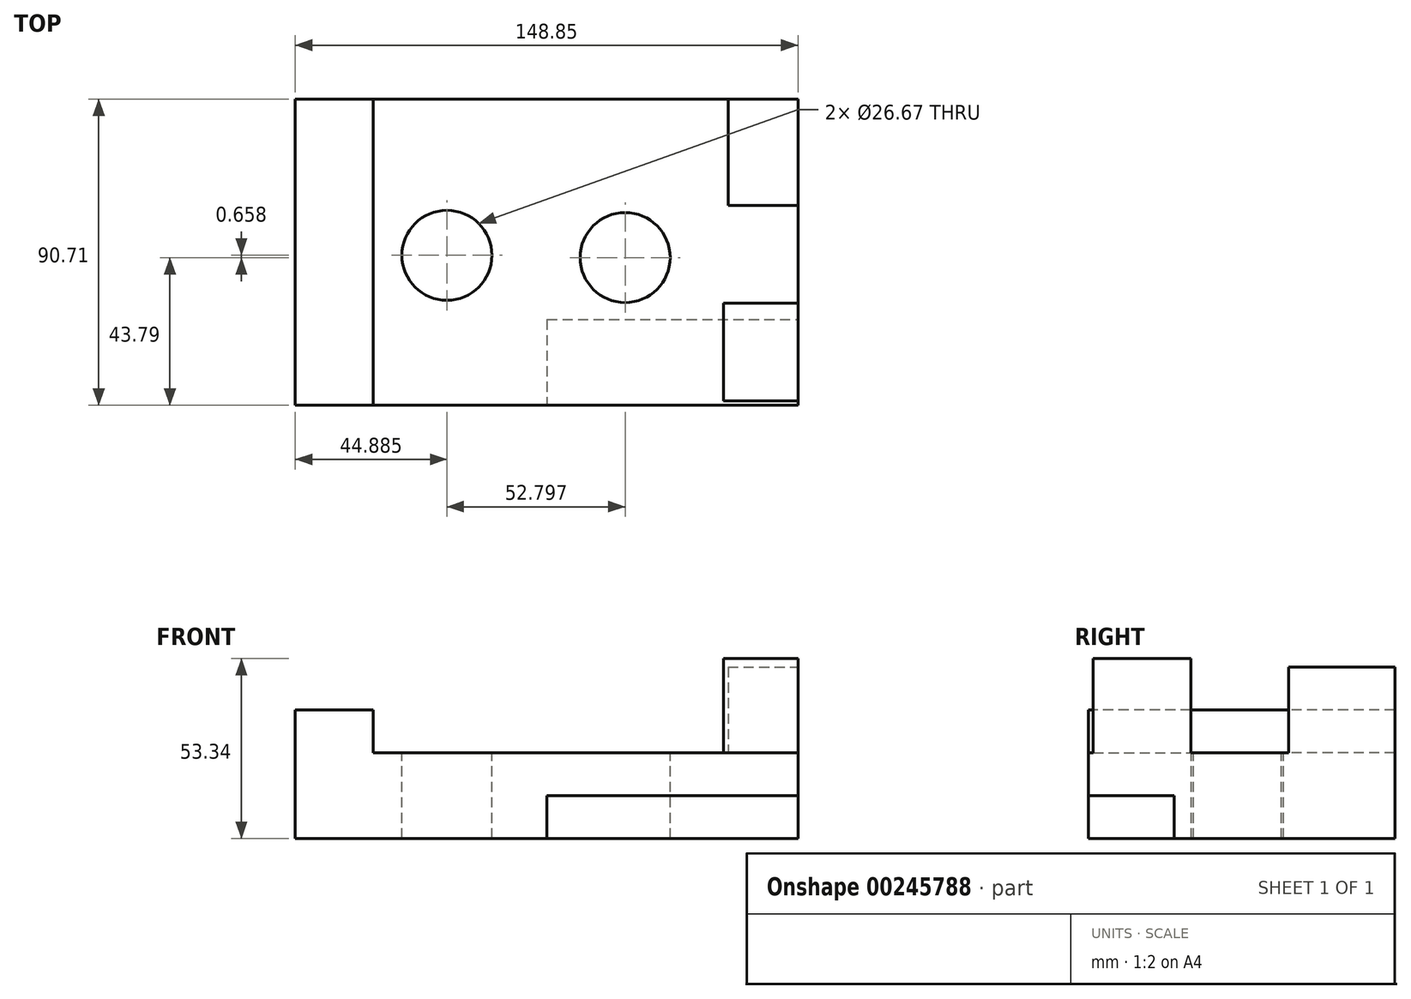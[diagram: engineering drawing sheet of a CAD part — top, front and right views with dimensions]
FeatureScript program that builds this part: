
annotation { "Feature Type Name" : "Feature", "Feature Type Description" : "" }
export const myFeature = defineFeature(function(context is Context, id is Id, definition is map)
    precondition{}
    {
        {
            var Q0;
            Q0=qCreatedBy(makeId("Top.planeOp"),FACE);
            var sketch = newSketch(context, id + "F0", { "sketchPlane" : qUnion([Q0])});
            skLineSegment(sketch, "E0.bottom", {"start": v(-74.54, 36.98) * mm, "end": v(74.31, 36.98) * mm});
            skLineSegment(sketch, "E0.top", {"start": v(-74.54, -53.73) * mm, "end": v(74.31, -53.73) * mm});
            skLineSegment(sketch, "E0.left", {"start": v(-74.54, 36.98) * mm, "end": v(-74.54, -53.73) * mm});
            skLineSegment(sketch, "E0.right", {"start": v(74.31, 36.98) * mm, "end": v(74.31, -53.73) * mm});
            skSolve(sketch);
        }
        {
            var Q0;
            Q0=makeQuery(id+"F0.imprint","IMPRINT",FACE,{"disambiguationData":[TD([[makeQuery(id+"F0.imprint","IMPRINT",EDGE,{"derivedFrom":sQuery(id+"F0.wireOp",EDGE,"E0.bottom")}),-1.0]])]});
            extrude(context, id + "F1", {"entities" : qUnion([Q0]), "depth" : 25.4 * mm});
        }
        {
            var Q0;
            Q0=makeQuery(id+"F1.opExtrude","SWEPT_FACE",FACE,{"disambiguationData":[OSD([sQuery(id+"F0.wireOp",EDGE,"E0.top")])]});
            var sketch = newSketch(context, id + "F2", { "sketchPlane" : qUnion([Q0])});
            skLineSegment(sketch, "E1.bottom", {"start": v(0, 0) * mm, "end": v(74.31, 0) * mm});
            skLineSegment(sketch, "E1.top", {"start": v(0, 12.7) * mm, "end": v(74.31, 12.7) * mm});
            skLineSegment(sketch, "E1.left", {"start": v(0, 0) * mm, "end": v(0, 12.7) * mm});
            skLineSegment(sketch, "E1.right", {"start": v(74.31, 0) * mm, "end": v(74.31, 12.7) * mm});
            skSolve(sketch);
        }
        {
            var Q0;
            Q0=makeQuery(id+"F2.imprint","IMPRINT",FACE,{"disambiguationData":[TD([[makeQuery(id+"F2.imprint","IMPRINT",EDGE,{"derivedFrom":sQuery(id+"F2.wireOp",EDGE,"E1.bottom")}),1.0]])]});
            extrude(context, id + "F3", {"entities" : qUnion([Q0]), "operationType" : NewBodyOperationType.REMOVE, "oppositeDirection" : true, "depth" : 25.4 * mm});
        }
        {
            var Q0;
            Q0=makeQuery(id+"F1.opExtrude","CAP_FACE",FACE,{"disambiguationData":[OSD([sQuery(id+"F0.wireOp",EDGE,"E0.bottom"),sQuery(id+"F0.wireOp",EDGE,"E0.top"),sQuery(id+"F0.wireOp",EDGE,"E0.left"),sQuery(id+"F0.wireOp",EDGE,"E0.right")])],"isStart":false});
            var sketch = newSketch(context, id + "F4", { "sketchPlane" : qUnion([Q0])});
            skLineSegment(sketch, "E2.bottom", {"start": v(-74.54, 36.98) * mm, "end": v(-51.52, 36.98) * mm});
            skLineSegment(sketch, "E2.top", {"start": v(-74.54, -53.73) * mm, "end": v(-51.52, -53.73) * mm});
            skLineSegment(sketch, "E2.left", {"start": v(-74.54, 36.98) * mm, "end": v(-74.54, -53.73) * mm});
            skLineSegment(sketch, "E2.right", {"start": v(-51.52, 36.98) * mm, "end": v(-51.52, -53.73) * mm});
            skSolve(sketch);
        }
        {
            var Q0;
            Q0=makeQuery(id+"F4.imprint","IMPRINT",FACE,{"disambiguationData":[TD([[makeQuery(id+"F4.imprint","IMPRINT",EDGE,{"derivedFrom":sQuery(id+"F4.wireOp",EDGE,"E2.bottom")}),-1.0]])]});
            extrude(context, id + "F5", {"entities" : qUnion([Q0]), "operationType" : NewBodyOperationType.ADD, "depth" : 12.7 * mm});
        }
        {
            var Q0;
            Q0=makeQuery(id+"F1.opExtrude","CAP_FACE",FACE,{"disambiguationData":[OSD([sQuery(id+"F0.wireOp",EDGE,"E0.bottom"),sQuery(id+"F0.wireOp",EDGE,"E0.top"),sQuery(id+"F0.wireOp",EDGE,"E0.left"),sQuery(id+"F0.wireOp",EDGE,"E0.right")])],"isStart":false});
            var sketch = newSketch(context, id + "F6", { "sketchPlane" : qUnion([Q0])});
            skLineSegment(sketch, "E3.bottom", {"start": v(74.31, 36.98) * mm, "end": v(53.61, 36.98) * mm});
            skLineSegment(sketch, "E3.top", {"start": v(74.31, 5.52) * mm, "end": v(53.61, 5.52) * mm});
            skLineSegment(sketch, "E3.left", {"start": v(74.31, 36.98) * mm, "end": v(74.31, 5.52) * mm});
            skLineSegment(sketch, "E3.right", {"start": v(53.61, 36.98) * mm, "end": v(53.61, 5.52) * mm});
            skSolve(sketch);
        }
        {
            var Q0;
            {var subQ2=sQuery(id+"F6.wireOp",EDGE,"E3.top");Q0=makeQuery(id+"F6.imprint","IMPRINT",FACE,{"disambiguationData":[TD([[makeQuery(id+"F6.imprint","IMPRINT",EDGE,{"derivedFrom":subQ2}),1.0]])]});}
            var sketch = newSketch(context, id + "F7", { "sketchPlane" : qUnion([Q0])});
            skLineSegment(sketch, "E4.bottom", {"start": v(74.31, -52.37) * mm, "end": v(52.22, -52.37) * mm});
            skLineSegment(sketch, "E4.top", {"start": v(74.31, -23.43) * mm, "end": v(52.22, -23.43) * mm});
            skLineSegment(sketch, "E4.left", {"start": v(74.31, -52.37) * mm, "end": v(74.31, -23.43) * mm});
            skLineSegment(sketch, "E4.right", {"start": v(52.22, -52.37) * mm, "end": v(52.22, -23.43) * mm});
            skSolve(sketch);
        }
        {
            var Q0;
            Q0=makeQuery(id+"F6.imprint","IMPRINT",FACE,{"disambiguationData":[TD([[makeQuery(id+"F6.imprint","IMPRINT",EDGE,{"derivedFrom":sQuery(id+"F6.wireOp",EDGE,"E3.bottom")}),-1.0]])]});
            extrude(context, id + "F8", {"entities" : qUnion([Q0]), "operationType" : NewBodyOperationType.ADD, "depth" : 25.4 * mm});
        }
        {
            var Q0;
            Q0=makeQuery(id+"F7.imprint","IMPRINT",FACE,{"disambiguationData":[TD([[makeQuery(id+"F7.imprint","IMPRINT",EDGE,{"derivedFrom":sQuery(id+"F7.wireOp",EDGE,"E4.bottom")}),-1.0]])]});
            extrude(context, id + "F9", {"entities" : qUnion([Q0]), "operationType" : NewBodyOperationType.ADD, "depth" : 27.94 * mm});
        }
        {
            var Q0;
            Q0=makeQuery(id+"F1.opExtrude","CAP_FACE",FACE,{"disambiguationData":[OSD([sQuery(id+"F0.wireOp",EDGE,"E0.bottom"),sQuery(id+"F0.wireOp",EDGE,"E0.top"),sQuery(id+"F0.wireOp",EDGE,"E0.left"),sQuery(id+"F0.wireOp",EDGE,"E0.right")])],"isStart":false});
            var sketch = newSketch(context, id + "F10", { "sketchPlane" : qUnion([Q0])});
            skCircle(sketch, "E5", {"center": v(-29.89, -8.95) * mm, "radius": 13.3 * mm});
            skSolve(sketch);
        }
        {
            var Q0;
            Q0=makeQuery(id+"F10.imprint","IMPRINT",FACE,{"disambiguationData":[TD([[makeQuery(id+"F10.imprint","IMPRINT",EDGE,{"derivedFrom":sQuery(id+"F10.wireOp",EDGE,"E5")}),-1.0]])]});
            var sketch = newSketch(context, id + "F11", { "sketchPlane" : qUnion([Q0])});
            skLineSegment(sketch, "E6", {"start": v(-29.65, -9.28) * mm, "end": v(-79.9, -9.28) * mm});
            skLineSegment(sketch, "E7", {"start": v(-29.65, -9.28) * mm, "end": v(-29.65, 33.8) * mm});
            skLineSegment(sketch, "E8", {"start": v(-29.65, -9.28) * mm, "end": v(-27.8, -51.71) * mm});
            skLineSegment(sketch, "E9", {"start": v(-29.65, -9.28) * mm, "end": v(4.54, -9.28) * mm});
            skSolve(sketch);
        }
        {
            var Q0;
            Q0=sQuery(id+"F11.wireOp",VERTEX,"E6.start");
            var Q1;
            Q1=makeQuery(id+"F1.opExtrude","SWEPT_BODY",BODY,{"disambiguationData":[OSD([sQuery(id+"F0.wireOp",EDGE,"E0.bottom"),sQuery(id+"F0.wireOp",EDGE,"E0.top"),sQuery(id+"F0.wireOp",EDGE,"E0.left"),sQuery(id+"F0.wireOp",EDGE,"E0.right")])]});
            hole(context, id + "F12", {"style" : HoleStyle.SIMPLE, "endStyle" : HoleEndStyle.THROUGH, "holeDiameter" : 26.67 * mm, "tappedDepth" : 12.7 * mm, "tapClearance" : 3, "locations" : qUnion([Q0]), "scope" : qUnion([Q1])});
        }
        {
            var Q0;
            Q0=makeQuery(id+"F10.imprint","IMPRINT",FACE,{"disambiguationData":[TD([[makeQuery(id+"F10.imprint","IMPRINT",EDGE,{"derivedFrom":sQuery(id+"F10.wireOp",EDGE,"E5")}),-1.0]])]});
            var sketch = newSketch(context, id + "F13", { "sketchPlane" : qUnion([Q0])});
            skLineSegment(sketch, "E10", {"start": v(23.14, -9.94) * mm, "end": v(23.14, 36.44) * mm});
            skLineSegment(sketch, "E11", {"start": v(23.14, -9.94) * mm, "end": v(0, -9.94) * mm});
            skLineSegment(sketch, "E12", {"start": v(23.14, -9.94) * mm, "end": v(23.14, -44.48) * mm});
            skLineSegment(sketch, "E13", {"start": v(23.14, -9.94) * mm, "end": v(47.33, -9.94) * mm});
            skSolve(sketch);
        }
        {
            var Q0;
            Q0=sQuery(id+"F13.wireOp",VERTEX,"E13.start");
            var Q1;
            Q1=makeQuery(id+"F1.opExtrude","SWEPT_BODY",BODY,{"disambiguationData":[OSD([sQuery(id+"F0.wireOp",EDGE,"E0.bottom"),sQuery(id+"F0.wireOp",EDGE,"E0.top"),sQuery(id+"F0.wireOp",EDGE,"E0.left"),sQuery(id+"F0.wireOp",EDGE,"E0.right")])]});
            hole(context, id + "F14", {"style" : HoleStyle.SIMPLE, "endStyle" : HoleEndStyle.THROUGH, "holeDiameter" : 26.67 * mm, "tappedDepth" : 12.7 * mm, "tapClearance" : 3, "locations" : qUnion([Q0]), "scope" : qUnion([Q1])});
        }
    });
